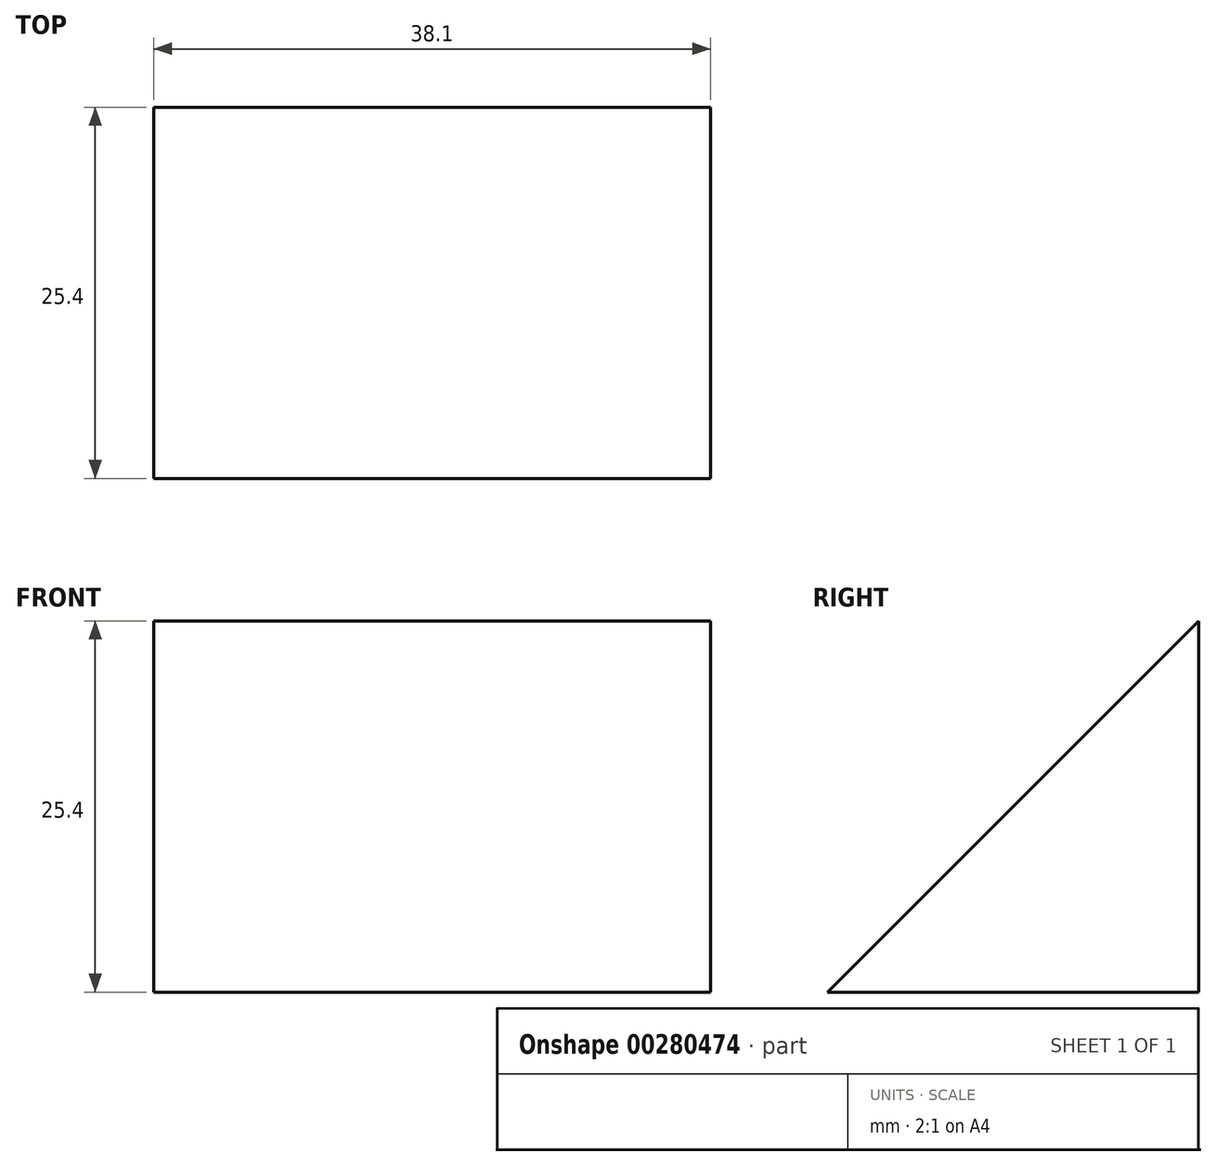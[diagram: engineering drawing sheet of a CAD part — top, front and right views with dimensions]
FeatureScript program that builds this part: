
annotation { "Feature Type Name" : "Feature", "Feature Type Description" : "" }
export const myFeature = defineFeature(function(context is Context, id is Id, definition is map)
    precondition{}
    {
        {
            var Q0;
            Q0=qCreatedBy(makeId("Right.planeOp"),FACE);
            var sketch = newSketch(context, id + "F0", { "sketchPlane" : qUnion([Q0])});
            skLineSegment(sketch, "E0", {"start": v(0, 0) * mm, "end": v(0, 25.4) * mm});
            skLineSegment(sketch, "E1", {"start": v(0, 25.4) * mm, "end": v(-25.4, 0) * mm});
            skLineSegment(sketch, "E2", {"start": v(-25.4, 0) * mm, "end": v(0, 0) * mm});
            skSolve(sketch);
        }
        {
            var Q0;
            Q0=makeQuery(id+"F0.imprint","IMPRINT",FACE,{"disambiguationData":[TD([[makeQuery(id+"F0.imprint","IMPRINT",EDGE,{"derivedFrom":sQuery(id+"F0.wireOp",EDGE,"E0")}),1.0]])]});
            extrude(context, id + "F1", {"entities" : qUnion([Q0]), "oppositeDirection" : true, "depth" : 38.1 * mm});
        }
    });
